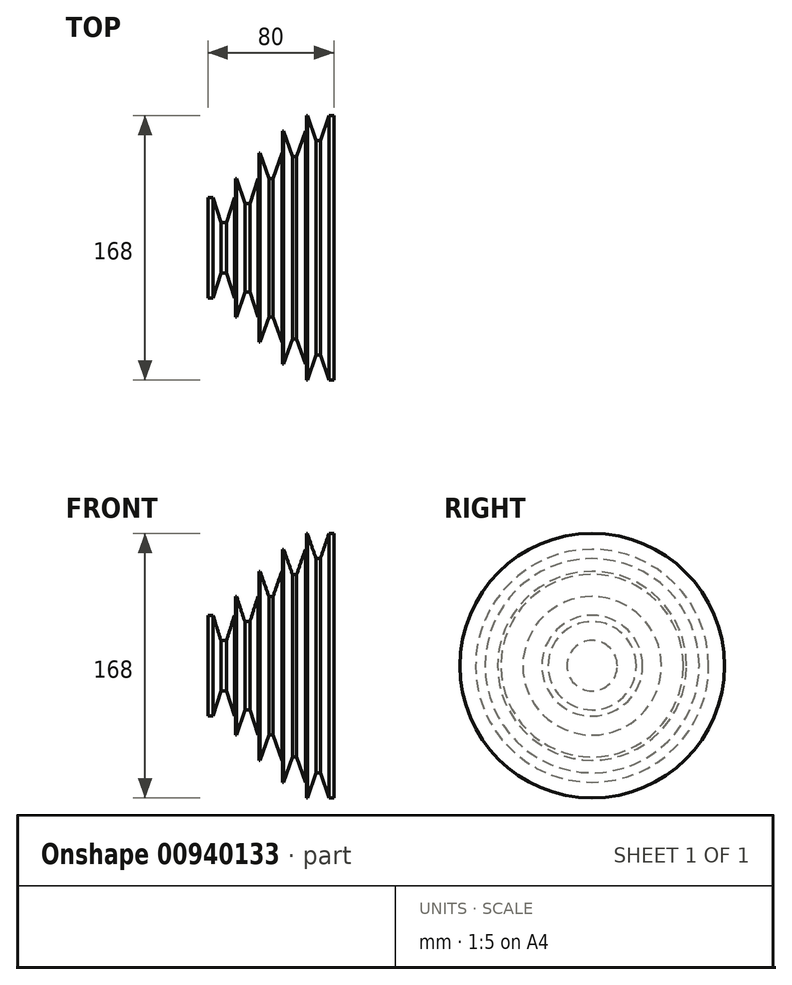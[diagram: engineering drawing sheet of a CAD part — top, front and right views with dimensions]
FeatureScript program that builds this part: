
annotation { "Feature Type Name" : "Feature", "Feature Type Description" : "" }
export const myFeature = defineFeature(function(context is Context, id is Id, definition is map)
    precondition{}
    {
        {
            var Q0;
            Q0=qCreatedBy(makeId("Front.planeOp"),FACE);
            var sketch = newSketch(context, id + "F0", { "sketchPlane" : qUnion([Q0])});
            skLineSegment(sketch, "E0", {"start": v(0, 0) * mm, "end": v(80, 0) * mm});
            skLineSegment(sketch, "E1", {"start": v(0, 0) * mm, "end": v(0, 32) * mm});
            skLineSegment(sketch, "E2", {"start": v(0, 84) * mm, "end": v(62.5, 84) * mm, "construction": true});
            skLineSegment(sketch, "E3", {"start": v(80, 84) * mm, "end": v(80, 0) * mm});
            skLineSegment(sketch, "E4", {"start": v(0, 16) * mm, "end": v(8.17, 16) * mm, "construction": true});
            skLineSegment(sketch, "E5", {"start": v(0, 28) * mm, "end": v(4.5, 28) * mm, "construction": true});
            skLineSegment(sketch, "E6", {"start": v(0, 32) * mm, "end": v(3.28, 32) * mm});
            skLineSegment(sketch, "E7", {"start": v(0, 40) * mm, "end": v(80, 40) * mm, "construction": true});
            skLineSegment(sketch, "E8", {"start": v(0, 44) * mm, "end": v(17.5, 44) * mm, "construction": true});
            skLineSegment(sketch, "E9", {"start": v(0, 56) * mm, "end": v(80, 56) * mm, "construction": true});
            skLineSegment(sketch, "E10", {"start": v(0, 60) * mm, "end": v(32.5, 60) * mm, "construction": true});
            skLineSegment(sketch, "E11", {"start": v(4.5, 0) * mm, "end": v(4.5, 84) * mm, "construction": true});
            skLineSegment(sketch, "E12", {"start": v(15.5, 0) * mm, "end": v(15.5, 84) * mm, "construction": true});
            skLineSegment(sketch, "E13", {"start": v(17.5, 0) * mm, "end": v(17.5, 32) * mm, "construction": true});
            skLineSegment(sketch, "E14", {"start": v(19.5, 0) * mm, "end": v(19.5, 84) * mm, "construction": true});
            skLineSegment(sketch, "E15", {"start": v(30.5, 0) * mm, "end": v(30.5, 84) * mm, "construction": true});
            skLineSegment(sketch, "E16", {"start": v(32.5, 0) * mm, "end": v(32.5, 44) * mm, "construction": true});
            skLineSegment(sketch, "E17", {"start": v(34.5, 0) * mm, "end": v(34.5, 84) * mm, "construction": true});
            skLineSegment(sketch, "E18", {"start": v(45.5, 0) * mm, "end": v(45.5, 84) * mm, "construction": true});
            skLineSegment(sketch, "E19", {"start": v(47.5, 0) * mm, "end": v(47.5, 60) * mm, "construction": true});
            skLineSegment(sketch, "E20", {"start": v(49.5, 0) * mm, "end": v(49.5, 84) * mm, "construction": true});
            skLineSegment(sketch, "E21", {"start": v(60.5, 0) * mm, "end": v(60.5, 84) * mm, "construction": true});
            skLineSegment(sketch, "E22", {"start": v(62.5, 0) * mm, "end": v(62.5, 74) * mm, "construction": true});
            skLineSegment(sketch, "E23", {"start": v(64.5, 0) * mm, "end": v(64.5, 84) * mm, "construction": true});
            skLineSegment(sketch, "E24", {"start": v(75.5, 0) * mm, "end": v(75.5, 84) * mm, "construction": true});
            skLineSegment(sketch, "E25", {"start": v(4.5, 28) * mm, "end": v(8.17, 16) * mm});
            skLineSegment(sketch, "E26", {"start": v(15.5, 28) * mm, "end": v(11.83, 16) * mm});
            skLineSegment(sketch, "E27", {"start": v(4.5, 28) * mm, "end": v(3.28, 32) * mm});
            skLineSegment(sketch, "E28", {"start": v(15.5, 28) * mm, "end": v(16.72, 32) * mm});
            skLineSegment(sketch, "E29", {"start": v(19.5, 40) * mm, "end": v(23.4, 28) * mm});
            skLineSegment(sketch, "E30", {"start": v(30.5, 40) * mm, "end": v(26.6, 28) * mm});
            skLineSegment(sketch, "E31", {"start": v(19.5, 40) * mm, "end": v(18.2, 44) * mm});
            skLineSegment(sketch, "E32", {"start": v(30.5, 40) * mm, "end": v(31.8, 44) * mm});
            skLineSegment(sketch, "E33", {"start": v(34.5, 56) * mm, "end": v(38.63, 44) * mm});
            skLineSegment(sketch, "E34", {"start": v(45.5, 56) * mm, "end": v(41.37, 44) * mm});
            skLineSegment(sketch, "E35", {"start": v(34.5, 56) * mm, "end": v(33.12, 60) * mm});
            skLineSegment(sketch, "E36", {"start": v(45.5, 56) * mm, "end": v(46.88, 60) * mm});
            skLineSegment(sketch, "E37", {"start": v(0, 58) * mm, "end": v(53.63, 58) * mm, "construction": true});
            skLineSegment(sketch, "E38", {"start": v(0, 70) * mm, "end": v(80, 70) * mm, "construction": true});
            skLineSegment(sketch, "E39", {"start": v(0, 74) * mm, "end": v(47.5, 74) * mm, "construction": true});
            skLineSegment(sketch, "E40", {"start": v(49.5, 70) * mm, "end": v(53.63, 58) * mm});
            skLineSegment(sketch, "E41", {"start": v(60.5, 70) * mm, "end": v(56.37, 58) * mm});
            skLineSegment(sketch, "E42", {"start": v(49.5, 70) * mm, "end": v(48.12, 74) * mm});
            skLineSegment(sketch, "E43", {"start": v(60.5, 70) * mm, "end": v(61.88, 74) * mm});
            skLineSegment(sketch, "E44", {"start": v(0, 80) * mm, "end": v(80, 80) * mm, "construction": true});
            skLineSegment(sketch, "E45", {"start": v(0, 68) * mm, "end": v(68.63, 68) * mm, "construction": true});
            skLineSegment(sketch, "E46", {"start": v(64.5, 80) * mm, "end": v(68.63, 68) * mm});
            skLineSegment(sketch, "E47", {"start": v(75.5, 80) * mm, "end": v(71.37, 68) * mm});
            skLineSegment(sketch, "E48", {"start": v(64.5, 80) * mm, "end": v(63.12, 84) * mm});
            skLineSegment(sketch, "E49", {"start": v(75.5, 80) * mm, "end": v(76.88, 84) * mm});
            skLineSegment(sketch, "E50", {"start": v(0, 32) * mm, "end": v(0, 84) * mm, "construction": true});
            skLineSegment(sketch, "E51", {"start": v(3.28, 32) * mm, "end": v(16.72, 32) * mm, "construction": true});
            skLineSegment(sketch, "E52", {"start": v(4.5, 28) * mm, "end": v(15.5, 28) * mm, "construction": true});
            skLineSegment(sketch, "E53", {"start": v(16.72, 32) * mm, "end": v(17.5, 32) * mm});
            skLineSegment(sketch, "E54", {"start": v(17.5, 32) * mm, "end": v(80, 32) * mm, "construction": true});
            skLineSegment(sketch, "E55", {"start": v(17.5, 32) * mm, "end": v(17.5, 44) * mm});
            skLineSegment(sketch, "E56", {"start": v(15.5, 28) * mm, "end": v(23.4, 28) * mm, "construction": true});
            skLineSegment(sketch, "E57", {"start": v(8.17, 16) * mm, "end": v(11.83, 16) * mm});
            skLineSegment(sketch, "E58", {"start": v(11.83, 16) * mm, "end": v(80, 16) * mm, "construction": true});
            skLineSegment(sketch, "E59", {"start": v(23.4, 28) * mm, "end": v(26.6, 28) * mm});
            skLineSegment(sketch, "E60", {"start": v(26.6, 28) * mm, "end": v(80, 28) * mm, "construction": true});
            skLineSegment(sketch, "E61", {"start": v(17.5, 44) * mm, "end": v(17.5, 84) * mm, "construction": true});
            skLineSegment(sketch, "E62", {"start": v(17.5, 44) * mm, "end": v(18.2, 44) * mm});
            skLineSegment(sketch, "E63", {"start": v(18.2, 44) * mm, "end": v(31.8, 44) * mm, "construction": true});
            skLineSegment(sketch, "E64", {"start": v(31.8, 44) * mm, "end": v(32.5, 44) * mm});
            skLineSegment(sketch, "E65", {"start": v(32.5, 44) * mm, "end": v(32.5, 60) * mm});
            skLineSegment(sketch, "E66", {"start": v(32.5, 44) * mm, "end": v(38.63, 44) * mm, "construction": true});
            skLineSegment(sketch, "E67", {"start": v(38.63, 44) * mm, "end": v(41.37, 44) * mm});
            skLineSegment(sketch, "E68", {"start": v(41.37, 44) * mm, "end": v(80, 44) * mm, "construction": true});
            skLineSegment(sketch, "E69", {"start": v(53.63, 58) * mm, "end": v(56.37, 58) * mm});
            skLineSegment(sketch, "E70", {"start": v(56.37, 58) * mm, "end": v(80, 58) * mm, "construction": true});
            skLineSegment(sketch, "E71", {"start": v(47.5, 60) * mm, "end": v(47.5, 60) * mm});
            skLineSegment(sketch, "E72", {"start": v(32.5, 60) * mm, "end": v(33.12, 60) * mm});
            skLineSegment(sketch, "E73", {"start": v(32.5, 60) * mm, "end": v(32.5, 84) * mm, "construction": true});
            skLineSegment(sketch, "E74", {"start": v(33.12, 60) * mm, "end": v(46.88, 60) * mm, "construction": true});
            skLineSegment(sketch, "E75", {"start": v(46.88, 60) * mm, "end": v(47.5, 60) * mm});
            skLineSegment(sketch, "E76", {"start": v(47.5, 60) * mm, "end": v(47.5, 74) * mm});
            skLineSegment(sketch, "E77", {"start": v(47.5, 60) * mm, "end": v(80, 60) * mm, "construction": true});
            skLineSegment(sketch, "E78", {"start": v(68.63, 68) * mm, "end": v(71.37, 68) * mm});
            skLineSegment(sketch, "E79", {"start": v(71.37, 68) * mm, "end": v(80, 68) * mm, "construction": true});
            skLineSegment(sketch, "E80", {"start": v(62.5, 74) * mm, "end": v(62.5, 84) * mm});
            skLineSegment(sketch, "E81", {"start": v(47.5, 74) * mm, "end": v(48.12, 74) * mm});
            skLineSegment(sketch, "E82", {"start": v(47.5, 74) * mm, "end": v(47.5, 84) * mm, "construction": true});
            skLineSegment(sketch, "E83", {"start": v(48.12, 74) * mm, "end": v(61.88, 74) * mm, "construction": true});
            skLineSegment(sketch, "E84", {"start": v(61.88, 74) * mm, "end": v(62.5, 74) * mm});
            skLineSegment(sketch, "E85", {"start": v(62.5, 74) * mm, "end": v(80, 74) * mm, "construction": true});
            skLineSegment(sketch, "E86", {"start": v(62.5, 84) * mm, "end": v(63.12, 84) * mm});
            skLineSegment(sketch, "E87", {"start": v(63.12, 84) * mm, "end": v(76.88, 84) * mm, "construction": true});
            skLineSegment(sketch, "E88", {"start": v(76.88, 84) * mm, "end": v(80, 84) * mm});
            skSolve(sketch);
        }
        {
            var Q0;
            Q0=makeQuery(id+"F0.imprint","IMPRINT",FACE,{"disambiguationData":[TD([[makeQuery(id+"F0.imprint","IMPRINT",EDGE,{"derivedFrom":sQuery(id+"F0.wireOp",EDGE,"E0")}),1.0]])]});
            var Q1;
            Q1=sQuery(id+"F0.wireOp",EDGE,"E0");
            revolve(context, id + "F1", {"surfaceOperationType" : NewSurfaceOperationType.NEW, "entities" : qUnion([Q0]), "axis" : qUnion([Q1]), "revolveType" : RevolveType.FULL});
        }
    });
